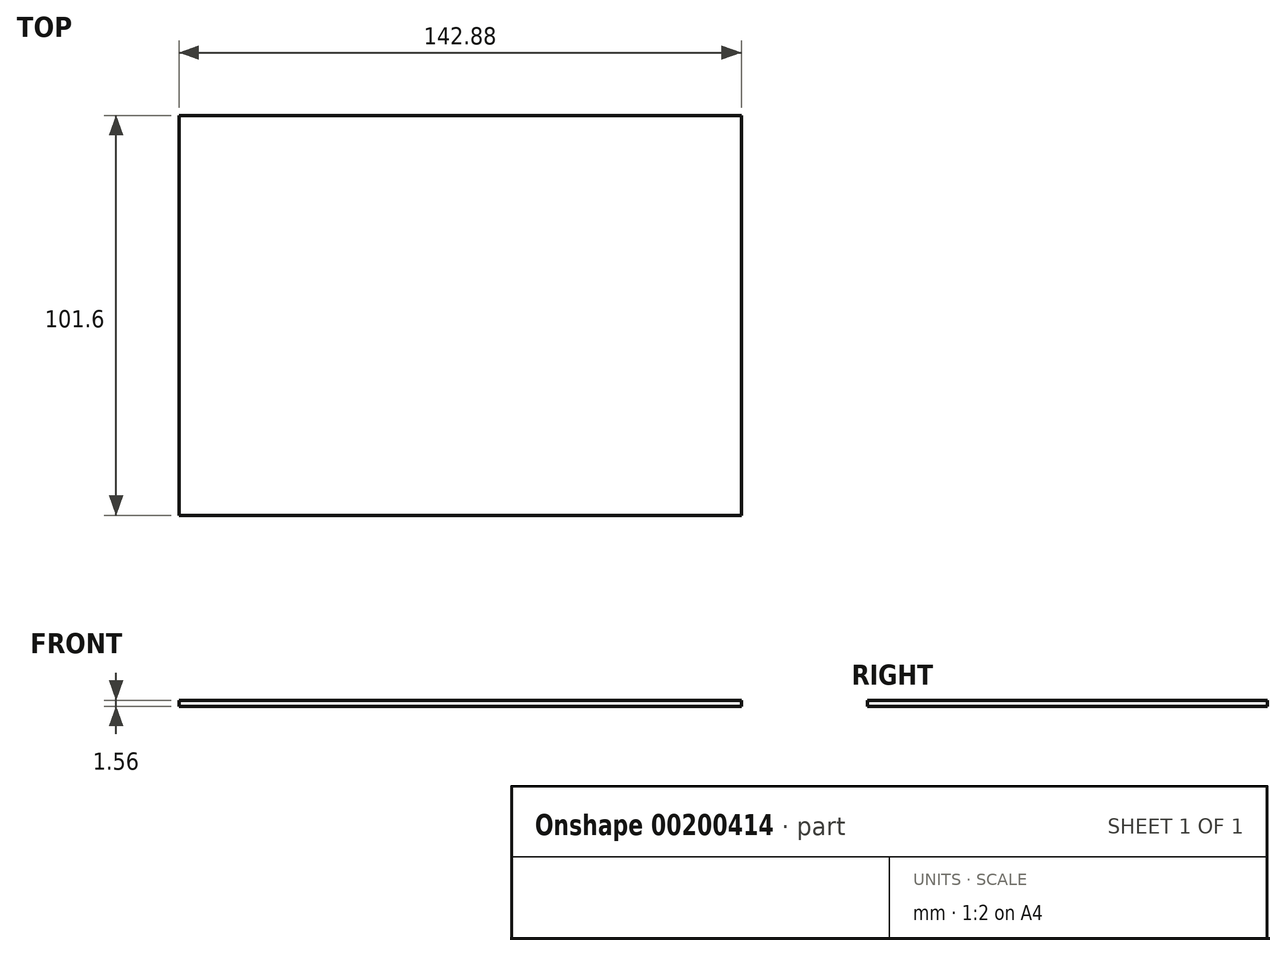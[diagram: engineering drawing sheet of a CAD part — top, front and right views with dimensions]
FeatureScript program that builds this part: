
annotation { "Feature Type Name" : "Feature", "Feature Type Description" : "" }
export const myFeature = defineFeature(function(context is Context, id is Id, definition is map)
    precondition{}
    {
        {
            var Q0;
            Q0=qCreatedBy(makeId("Top.planeOp"), FACE);
            var sketch = newSketch(context, id + "F0", { "sketchPlane" : qUnion([Q0])});
            skLineSegment(sketch, "E0.bottom", {"start": v(0, 0) * mm, "end": v(-142.87, 0) * mm});
            skLineSegment(sketch, "E0.top", {"start": v(0, -101.6) * mm, "end": v(-142.87, -101.6) * mm});
            skLineSegment(sketch, "E0.left", {"start": v(0, 0) * mm, "end": v(0, -101.6) * mm});
            skLineSegment(sketch, "E0.right", {"start": v(-142.88, 0) * mm, "end": v(-142.88, -101.6) * mm});
            skSolve(sketch);
        }
        {
            var Q0;
            Q0 = qSketchRegion(id + "F0", true);
            extrude(context, id + "F1", {"entities" : qUnion([Q0]), "depth" : (1 + (9 / 16)) * mm, "offsetDistance" : 25.4 * mm});
        }
    });
